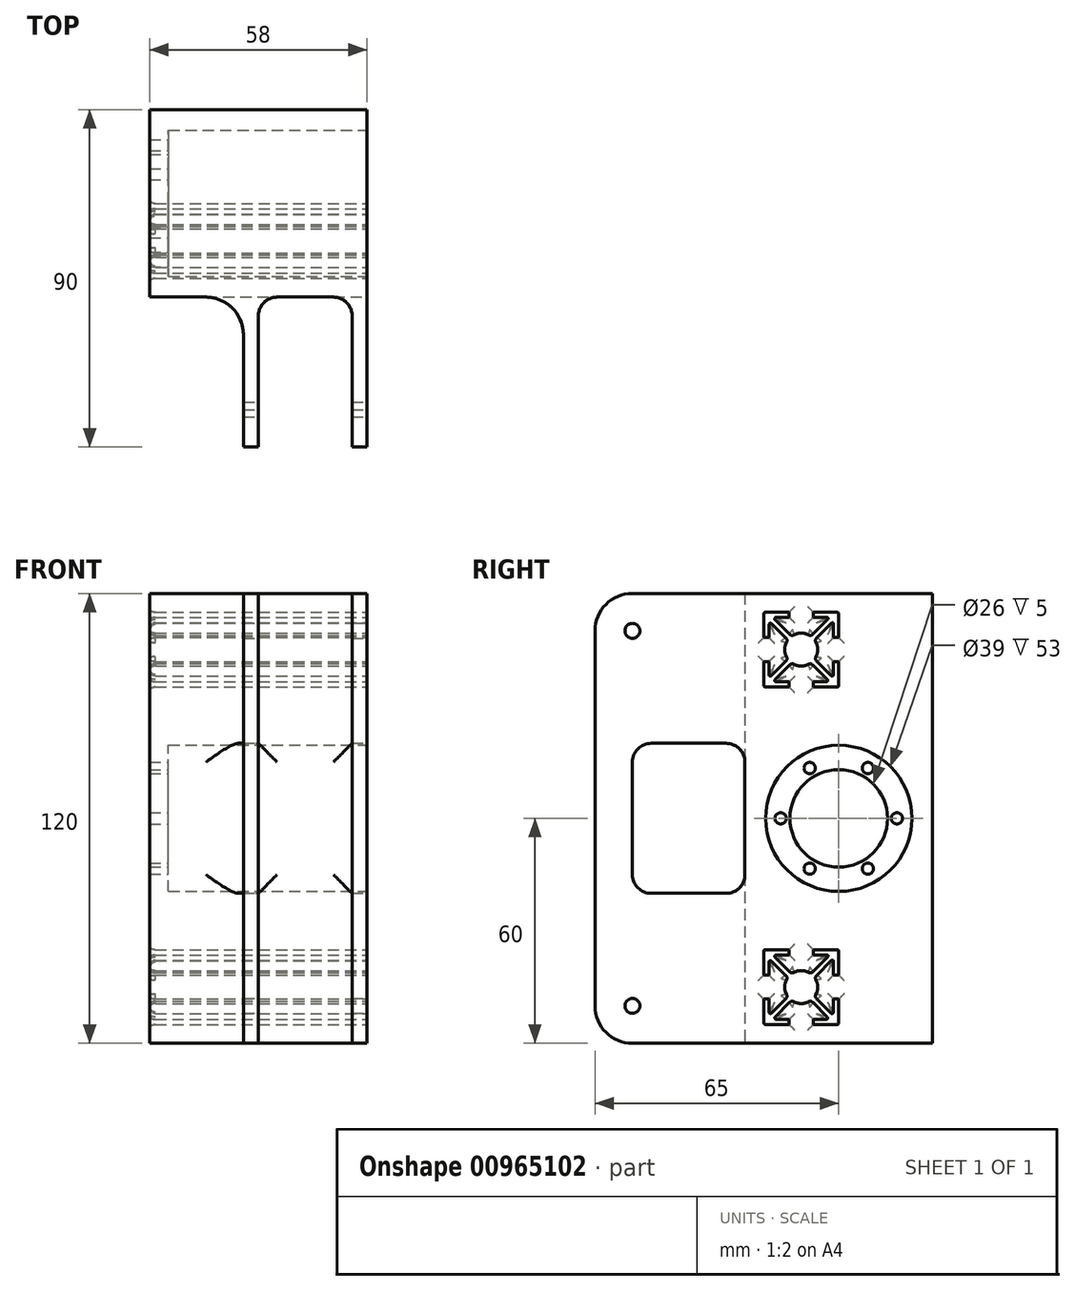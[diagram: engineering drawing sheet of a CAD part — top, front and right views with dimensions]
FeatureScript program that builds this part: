
annotation { "Feature Type Name" : "Feature", "Feature Type Description" : "" }
export const myFeature = defineFeature(function(context is Context, id is Id, definition is map)
    precondition{}
    {
        {
            var Q0;
            Q0=qCreatedBy(makeId("Top.planeOp"),FACE);
            var sketch = newSketch(context, id + "F0", { "sketchPlane" : qUnion([Q0])});
            skLineSegment(sketch, "E0", {"start": v(-25, 90) * mm, "end": v(33, 90) * mm});
            skLineSegment(sketch, "E1", {"start": v(33, 90) * mm, "end": v(33, 0) * mm});
            skLineSegment(sketch, "E2", {"start": v(33, 0) * mm, "end": v(29, 0) * mm});
            skLineSegment(sketch, "E3", {"start": v(29, 0) * mm, "end": v(29, 40) * mm});
            skLineSegment(sketch, "E4", {"start": v(29, 40) * mm, "end": v(4, 40) * mm});
            skLineSegment(sketch, "E5", {"start": v(4, 40) * mm, "end": v(4, 0) * mm});
            skLineSegment(sketch, "E6", {"start": v(4, 0) * mm, "end": v(0, 0) * mm});
            skLineSegment(sketch, "E7", {"start": v(0, 0) * mm, "end": v(0, 40) * mm});
            skLineSegment(sketch, "E8", {"start": v(0, 40) * mm, "end": v(-25, 40) * mm});
            skLineSegment(sketch, "E9", {"start": v(-25, 40) * mm, "end": v(-25, 90) * mm});
            skSolve(sketch);
        }
        {
            var Q0;
            Q0=makeQuery(id+"F0.imprint","IMPRINT",FACE,{"disambiguationData":[TD([[makeQuery(id+"F0.imprint","IMPRINT",EDGE,{"derivedFrom":sQuery(id+"F0.wireOp",EDGE,"VUWFp00N-zC5u-VRxy-L6zH-FIhfyABYxTeX")}),-1.0]])]});
            var Q1;
            Q1=makeQuery(id+"F0.imprint","IMPRINT",FACE,{"disambiguationData":[TD([[makeQuery(id+"F0.imprint","IMPRINT",EDGE,{"derivedFrom":sQuery(id+"F0.wireOp",EDGE,"E0")}),-1.0]])]});
            extrude(context, id + "F1", {"entities" : qUnion([Q0, Q1]), "depth" : 120 * mm, "offsetDistance" : 25 * mm});
        }
        {
            var Q0;
            Q0=makeQuery(id+"F1.opExtrude","SWEPT_FACE",FACE,{"disambiguationData":[OSD([sQuery(id+"F0.wireOp",EDGE,"E1")])]});
            var sketch = newSketch(context, id + "F2", { "sketchPlane" : qUnion([Q0])});
            skCircle(sketch, "E10", {"center": v(10, 110) * mm, "radius": 2 * mm});
            skCircle(sketch, "E11", {"center": v(10, 10) * mm, "radius": 2 * mm});
            skLineSegment(sketch, "E12.bottom", {"start": v(15, 40) * mm, "end": v(35, 40) * mm});
            skLineSegment(sketch, "E12.top", {"start": v(15, 80) * mm, "end": v(35, 80) * mm});
            skLineSegment(sketch, "E12.left", {"start": v(10, 45) * mm, "end": v(10, 75) * mm});
            skLineSegment(sketch, "E12.right", {"start": v(40, 45) * mm, "end": v(40, 75) * mm});
            skPoint(sketch, "E13.visualSharp", {"position": v(10, 40) * mm});
            skArc(sketch, "E13.filletArc", {"start": v(10, 45) * mm, "mid": v(11.46, 41.46) * mm, "end": v(15, 40) * mm});
            skPoint(sketch, "E14.visualSharp", {"position": v(10, 80) * mm});
            skArc(sketch, "E14.filletArc", {"start": v(15, 80) * mm, "mid": v(11.46, 78.54) * mm, "end": v(10, 75) * mm});
            skPoint(sketch, "E15.visualSharp", {"position": v(40, 80) * mm});
            skArc(sketch, "E15.filletArc", {"start": v(40, 75) * mm, "mid": v(38.54, 78.54) * mm, "end": v(35, 80) * mm});
            skPoint(sketch, "E16.visualSharp", {"position": v(40, 40) * mm});
            skArc(sketch, "E16.filletArc", {"start": v(35, 40) * mm, "mid": v(38.54, 41.46) * mm, "end": v(40, 45) * mm});
            skLineSegment(sketch, "E17.bottom", {"start": v(45, 5) * mm, "end": v(65, 5) * mm, "construction": true});
            skLineSegment(sketch, "E17.top", {"start": v(45, 25) * mm, "end": v(65, 25) * mm, "construction": true});
            skLineSegment(sketch, "E17.left", {"start": v(45, 5) * mm, "end": v(45, 25) * mm, "construction": true});
            skLineSegment(sketch, "E17.right", {"start": v(65, 5) * mm, "end": v(65, 25) * mm, "construction": true});
            skLineSegment(sketch, "E18", {"start": v(55, 25) * mm, "end": v(55, 5) * mm, "construction": true});
            skLineSegment(sketch, "E19", {"start": v(65, 15) * mm, "end": v(45, 15) * mm, "construction": true});
            skLineSegment(sketch, "E20", {"start": v(64.5, 25) * mm, "end": v(58.2, 25) * mm});
            skLineSegment(sketch, "E21", {"start": v(58.2, 25) * mm, "end": v(58.2, 23.6) * mm});
            skLineSegment(sketch, "E22", {"start": v(58.2, 23.6) * mm, "end": v(61.89, 23.6) * mm});
            skLineSegment(sketch, "E23", {"start": v(45, 5) * mm, "end": v(65, 25) * mm, "construction": true});
            skLineSegment(sketch, "E24", {"start": v(65, 5) * mm, "end": v(45, 25) * mm, "construction": true});
            skLineSegment(sketch, "E25", {"start": v(62.1, 23.09) * mm, "end": v(58.1, 19.08) * mm});
            skLineSegment(sketch, "E26", {"start": v(65, 18.2) * mm, "end": v(63.6, 18.2) * mm});
            skLineSegment(sketch, "E27", {"start": v(63.6, 18.2) * mm, "end": v(63.6, 21.89) * mm});
            skLineSegment(sketch, "E28", {"start": v(63.09, 22.1) * mm, "end": v(59.08, 18.1) * mm});
            skLineSegment(sketch, "E29", {"start": v(65, 5.5) * mm, "end": v(65, 11.8) * mm});
            skLineSegment(sketch, "E30", {"start": v(65, 11.8) * mm, "end": v(63.6, 11.8) * mm});
            skLineSegment(sketch, "E31", {"start": v(63.6, 11.8) * mm, "end": v(63.6, 8.36) * mm});
            skLineSegment(sketch, "E32", {"start": v(62.92, 8.07) * mm, "end": v(59.08, 11.9) * mm});
            skLineSegment(sketch, "E33", {"start": v(58.2, 5) * mm, "end": v(58.2, 6.4) * mm});
            skLineSegment(sketch, "E34", {"start": v(58.2, 6.4) * mm, "end": v(61.64, 6.4) * mm});
            skLineSegment(sketch, "E35", {"start": v(61.93, 7.08) * mm, "end": v(58.1, 10.92) * mm});
            skLineSegment(sketch, "E36", {"start": v(51.8, 5) * mm, "end": v(51.8, 6.4) * mm});
            skLineSegment(sketch, "E37", {"start": v(51.8, 6.4) * mm, "end": v(48.36, 6.4) * mm});
            skLineSegment(sketch, "E38", {"start": v(48.07, 7.08) * mm, "end": v(51.9, 10.92) * mm});
            skLineSegment(sketch, "E39", {"start": v(51.8, 5) * mm, "end": v(45.5, 5) * mm});
            skLineSegment(sketch, "E40", {"start": v(45, 11.8) * mm, "end": v(46.4, 11.8) * mm});
            skLineSegment(sketch, "E41", {"start": v(46.4, 11.8) * mm, "end": v(46.4, 8.36) * mm});
            skLineSegment(sketch, "E42", {"start": v(47.08, 8.07) * mm, "end": v(50.92, 11.9) * mm});
            skLineSegment(sketch, "E43", {"start": v(45, 24.5) * mm, "end": v(45, 18.2) * mm});
            skLineSegment(sketch, "E44", {"start": v(45, 18.2) * mm, "end": v(46.4, 18.2) * mm});
            skLineSegment(sketch, "E45", {"start": v(46.4, 18.2) * mm, "end": v(46.4, 21.64) * mm});
            skLineSegment(sketch, "E46", {"start": v(47.08, 21.93) * mm, "end": v(50.92, 18.1) * mm});
            skLineSegment(sketch, "E47", {"start": v(51.8, 25) * mm, "end": v(51.8, 23.6) * mm});
            skLineSegment(sketch, "E48", {"start": v(51.8, 23.6) * mm, "end": v(48.36, 23.6) * mm});
            skLineSegment(sketch, "E49", {"start": v(48.07, 22.92) * mm, "end": v(51.9, 19.08) * mm});
            skLineSegment(sketch, "E50", {"start": v(65, 18.2) * mm, "end": v(65, 24.5) * mm});
            skLineSegment(sketch, "E51", {"start": v(51.8, 25) * mm, "end": v(45.5, 25) * mm});
            skLineSegment(sketch, "E52", {"start": v(45, 11.8) * mm, "end": v(45, 5.5) * mm});
            skLineSegment(sketch, "E53", {"start": v(58.2, 5) * mm, "end": v(64.5, 5) * mm});
            skArc(sketch, "E54", {"start": v(56.9, 18.92) * mm, "mid": v(55, 19.41) * mm, "end": v(53.1, 18.92) * mm});
            skArc(sketch, "E55", {"start": v(58.92, 13.1) * mm, "mid": v(59.41, 15) * mm, "end": v(58.92, 16.9) * mm});
            skArc(sketch, "E56", {"start": v(53.1, 11.08) * mm, "mid": v(55, 10.59) * mm, "end": v(56.9, 11.08) * mm});
            skArc(sketch, "E57", {"start": v(51.08, 16.9) * mm, "mid": v(50.59, 15) * mm, "end": v(51.08, 13.1) * mm});
            skPoint(sketch, "E58", {"position": v(55, 15) * mm});
            skPoint(sketch, "E59.visualSharp", {"position": v(47.39, 23.6) * mm});
            skArc(sketch, "E59.filletArc", {"start": v(48.36, 23.6) * mm, "mid": v(47.99, 23.35) * mm, "end": v(48.07, 22.92) * mm});
            skPoint(sketch, "E60.visualSharp", {"position": v(62.61, 23.6) * mm});
            skArc(sketch, "E60.filletArc", {"start": v(62.1, 23.09) * mm, "mid": v(62.16, 23.41) * mm, "end": v(61.89, 23.6) * mm});
            skPoint(sketch, "E61.visualSharp", {"position": v(63.6, 22.61) * mm});
            skArc(sketch, "E61.filletArc", {"start": v(63.6, 21.89) * mm, "mid": v(63.41, 22.16) * mm, "end": v(63.09, 22.1) * mm});
            skPoint(sketch, "E62.visualSharp", {"position": v(63.6, 7.39) * mm});
            skArc(sketch, "E62.filletArc", {"start": v(62.92, 8.07) * mm, "mid": v(63.35, 7.99) * mm, "end": v(63.6, 8.36) * mm});
            skPoint(sketch, "E63.visualSharp", {"position": v(62.61, 6.4) * mm});
            skArc(sketch, "E63.filletArc", {"start": v(61.64, 6.4) * mm, "mid": v(62.01, 6.65) * mm, "end": v(61.93, 7.08) * mm});
            skPoint(sketch, "E64.visualSharp", {"position": v(47.39, 6.4) * mm});
            skArc(sketch, "E64.filletArc", {"start": v(48.07, 7.08) * mm, "mid": v(47.99, 6.65) * mm, "end": v(48.36, 6.4) * mm});
            skPoint(sketch, "E65.visualSharp", {"position": v(46.4, 7.39) * mm});
            skArc(sketch, "E65.filletArc", {"start": v(46.4, 8.36) * mm, "mid": v(46.65, 7.99) * mm, "end": v(47.08, 8.07) * mm});
            skPoint(sketch, "E66.visualSharp", {"position": v(46.4, 22.61) * mm});
            skArc(sketch, "E66.filletArc", {"start": v(47.08, 21.93) * mm, "mid": v(46.65, 22.01) * mm, "end": v(46.4, 21.64) * mm});
            skPoint(sketch, "E67.visualSharp", {"position": v(52.49, 18.5) * mm});
            skArc(sketch, "E67.filletArc", {"start": v(51.9, 19.08) * mm, "mid": v(52.47, 18.8) * mm, "end": v(53.1, 18.92) * mm});
            skPoint(sketch, "E68.visualSharp", {"position": v(57.51, 18.5) * mm});
            skArc(sketch, "E68.filletArc", {"start": v(56.9, 18.92) * mm, "mid": v(57.53, 18.8) * mm, "end": v(58.1, 19.08) * mm});
            skPoint(sketch, "E69.visualSharp", {"position": v(58.5, 17.51) * mm});
            skArc(sketch, "E69.filletArc", {"start": v(59.08, 18.1) * mm, "mid": v(58.8, 17.53) * mm, "end": v(58.92, 16.9) * mm});
            skPoint(sketch, "E70.visualSharp", {"position": v(58.5, 12.49) * mm});
            skArc(sketch, "E70.filletArc", {"start": v(58.92, 13.1) * mm, "mid": v(58.8, 12.47) * mm, "end": v(59.08, 11.9) * mm});
            skPoint(sketch, "E71.visualSharp", {"position": v(57.51, 11.5) * mm});
            skArc(sketch, "E71.filletArc", {"start": v(58.1, 10.92) * mm, "mid": v(57.53, 11.2) * mm, "end": v(56.9, 11.08) * mm});
            skPoint(sketch, "E72.visualSharp", {"position": v(52.49, 11.5) * mm});
            skArc(sketch, "E72.filletArc", {"start": v(53.1, 11.08) * mm, "mid": v(52.47, 11.2) * mm, "end": v(51.9, 10.92) * mm});
            skPoint(sketch, "E73.visualSharp", {"position": v(51.5, 12.49) * mm});
            skArc(sketch, "E73.filletArc", {"start": v(50.92, 11.9) * mm, "mid": v(51.2, 12.47) * mm, "end": v(51.08, 13.1) * mm});
            skPoint(sketch, "E74.visualSharp", {"position": v(51.5, 17.51) * mm});
            skArc(sketch, "E74.filletArc", {"start": v(51.08, 16.9) * mm, "mid": v(51.2, 17.53) * mm, "end": v(50.92, 18.1) * mm});
            skPoint(sketch, "E75.visualSharp", {"position": v(45, 25) * mm});
            skArc(sketch, "E75.filletArc", {"start": v(45.5, 25) * mm, "mid": v(45.15, 24.85) * mm, "end": v(45, 24.5) * mm});
            skPoint(sketch, "E76.visualSharp", {"position": v(65, 25) * mm});
            skArc(sketch, "E76.filletArc", {"start": v(65, 24.5) * mm, "mid": v(64.85, 24.85) * mm, "end": v(64.5, 25) * mm});
            skPoint(sketch, "E77.visualSharp", {"position": v(65, 5) * mm});
            skArc(sketch, "E77.filletArc", {"start": v(64.5, 5) * mm, "mid": v(64.85, 5.15) * mm, "end": v(65, 5.5) * mm});
            skPoint(sketch, "E78.visualSharp", {"position": v(45, 5) * mm});
            skArc(sketch, "E78.filletArc", {"start": v(45, 5.5) * mm, "mid": v(45.15, 5.15) * mm, "end": v(45.5, 5) * mm});
            skLineSegment(sketch, "E79.bottom", {"start": v(45, 95) * mm, "end": v(65, 95) * mm, "construction": true});
            skLineSegment(sketch, "E79.top", {"start": v(45, 115) * mm, "end": v(65, 115) * mm, "construction": true});
            skLineSegment(sketch, "E79.left", {"start": v(45, 95) * mm, "end": v(45, 115) * mm, "construction": true});
            skLineSegment(sketch, "E79.right", {"start": v(65, 95) * mm, "end": v(65, 115) * mm, "construction": true});
            skLineSegment(sketch, "E80", {"start": v(55, 115) * mm, "end": v(55, 95) * mm, "construction": true});
            skLineSegment(sketch, "E81", {"start": v(65, 105) * mm, "end": v(45, 105) * mm, "construction": true});
            skLineSegment(sketch, "E82", {"start": v(64.5, 115) * mm, "end": v(58.2, 115) * mm});
            skLineSegment(sketch, "E83", {"start": v(58.2, 115) * mm, "end": v(58.2, 113.6) * mm});
            skLineSegment(sketch, "E84", {"start": v(58.2, 113.6) * mm, "end": v(61.89, 113.6) * mm});
            skLineSegment(sketch, "E85", {"start": v(45, 95) * mm, "end": v(65, 115) * mm, "construction": true});
            skLineSegment(sketch, "E86", {"start": v(65, 95) * mm, "end": v(45, 115) * mm, "construction": true});
            skLineSegment(sketch, "E87", {"start": v(62.1, 113.09) * mm, "end": v(58.1, 109.08) * mm});
            skLineSegment(sketch, "E88", {"start": v(65, 108.2) * mm, "end": v(63.6, 108.2) * mm});
            skLineSegment(sketch, "E89", {"start": v(63.6, 108.2) * mm, "end": v(63.6, 111.89) * mm});
            skLineSegment(sketch, "E90", {"start": v(63.09, 112.1) * mm, "end": v(59.08, 108.1) * mm});
            skLineSegment(sketch, "E91", {"start": v(65, 95.5) * mm, "end": v(65, 101.8) * mm});
            skLineSegment(sketch, "E92", {"start": v(65, 101.8) * mm, "end": v(63.6, 101.8) * mm});
            skLineSegment(sketch, "E93", {"start": v(63.6, 101.8) * mm, "end": v(63.6, 98.36) * mm});
            skLineSegment(sketch, "E94", {"start": v(62.92, 98.07) * mm, "end": v(59.08, 101.9) * mm});
            skLineSegment(sketch, "E95", {"start": v(58.2, 95) * mm, "end": v(58.2, 96.4) * mm});
            skLineSegment(sketch, "E96", {"start": v(58.2, 96.4) * mm, "end": v(61.64, 96.4) * mm});
            skLineSegment(sketch, "E97", {"start": v(61.93, 97.08) * mm, "end": v(58.1, 100.92) * mm});
            skLineSegment(sketch, "E98", {"start": v(51.8, 95) * mm, "end": v(51.8, 96.4) * mm});
            skLineSegment(sketch, "E99", {"start": v(51.8, 96.4) * mm, "end": v(48.36, 96.4) * mm});
            skLineSegment(sketch, "E100", {"start": v(48.07, 97.08) * mm, "end": v(51.9, 100.92) * mm});
            skLineSegment(sketch, "E101", {"start": v(51.8, 95) * mm, "end": v(45.5, 95) * mm});
            skLineSegment(sketch, "E102", {"start": v(45, 101.8) * mm, "end": v(46.4, 101.8) * mm});
            skLineSegment(sketch, "E103", {"start": v(46.4, 101.8) * mm, "end": v(46.4, 98.36) * mm});
            skLineSegment(sketch, "E104", {"start": v(47.08, 98.07) * mm, "end": v(50.92, 101.9) * mm});
            skLineSegment(sketch, "E105", {"start": v(45, 114.5) * mm, "end": v(45, 108.2) * mm});
            skLineSegment(sketch, "E106", {"start": v(45, 108.2) * mm, "end": v(46.4, 108.2) * mm});
            skLineSegment(sketch, "E107", {"start": v(46.4, 108.2) * mm, "end": v(46.4, 111.64) * mm});
            skLineSegment(sketch, "E108", {"start": v(47.08, 111.93) * mm, "end": v(50.92, 108.1) * mm});
            skLineSegment(sketch, "E109", {"start": v(51.8, 115) * mm, "end": v(51.8, 113.6) * mm});
            skLineSegment(sketch, "E110", {"start": v(51.8, 113.6) * mm, "end": v(48.36, 113.6) * mm});
            skLineSegment(sketch, "E111", {"start": v(48.07, 112.92) * mm, "end": v(51.9, 109.08) * mm});
            skLineSegment(sketch, "E112", {"start": v(65, 108.2) * mm, "end": v(65, 114.5) * mm});
            skLineSegment(sketch, "E113", {"start": v(51.8, 115) * mm, "end": v(45.5, 115) * mm});
            skLineSegment(sketch, "E114", {"start": v(45, 101.8) * mm, "end": v(45, 95.5) * mm});
            skLineSegment(sketch, "E115", {"start": v(58.2, 95) * mm, "end": v(64.5, 95) * mm});
            skArc(sketch, "E116", {"start": v(56.9, 108.92) * mm, "mid": v(55, 109.41) * mm, "end": v(53.1, 108.92) * mm});
            skArc(sketch, "E117", {"start": v(58.92, 103.1) * mm, "mid": v(59.41, 105) * mm, "end": v(58.92, 106.9) * mm});
            skArc(sketch, "E118", {"start": v(53.1, 101.08) * mm, "mid": v(55, 100.59) * mm, "end": v(56.9, 101.08) * mm});
            skArc(sketch, "E119", {"start": v(51.08, 106.9) * mm, "mid": v(50.59, 105) * mm, "end": v(51.08, 103.1) * mm});
            skPoint(sketch, "E120", {"position": v(55, 105) * mm});
            skPoint(sketch, "E121.visualSharp", {"position": v(47.39, 113.6) * mm});
            skArc(sketch, "E121.filletArc", {"start": v(48.36, 113.6) * mm, "mid": v(47.99, 113.35) * mm, "end": v(48.07, 112.92) * mm});
            skPoint(sketch, "E122.visualSharp", {"position": v(62.61, 113.6) * mm});
            skArc(sketch, "E122.filletArc", {"start": v(62.1, 113.09) * mm, "mid": v(62.16, 113.41) * mm, "end": v(61.89, 113.6) * mm});
            skPoint(sketch, "E123.visualSharp", {"position": v(63.6, 112.61) * mm});
            skArc(sketch, "E123.filletArc", {"start": v(63.6, 111.89) * mm, "mid": v(63.41, 112.16) * mm, "end": v(63.09, 112.1) * mm});
            skPoint(sketch, "E124.visualSharp", {"position": v(63.6, 97.39) * mm});
            skArc(sketch, "E124.filletArc", {"start": v(62.92, 98.07) * mm, "mid": v(63.35, 97.99) * mm, "end": v(63.6, 98.36) * mm});
            skPoint(sketch, "E125.visualSharp", {"position": v(62.61, 96.4) * mm});
            skArc(sketch, "E125.filletArc", {"start": v(61.64, 96.4) * mm, "mid": v(62.01, 96.65) * mm, "end": v(61.93, 97.08) * mm});
            skPoint(sketch, "E126.visualSharp", {"position": v(47.39, 96.4) * mm});
            skArc(sketch, "E126.filletArc", {"start": v(48.07, 97.08) * mm, "mid": v(47.99, 96.65) * mm, "end": v(48.36, 96.4) * mm});
            skPoint(sketch, "E127.visualSharp", {"position": v(46.4, 97.39) * mm});
            skArc(sketch, "E127.filletArc", {"start": v(46.4, 98.36) * mm, "mid": v(46.65, 97.99) * mm, "end": v(47.08, 98.07) * mm});
            skPoint(sketch, "E128.visualSharp", {"position": v(46.4, 112.61) * mm});
            skArc(sketch, "E128.filletArc", {"start": v(47.08, 111.93) * mm, "mid": v(46.65, 112.01) * mm, "end": v(46.4, 111.64) * mm});
            skPoint(sketch, "E129.visualSharp", {"position": v(52.49, 108.5) * mm});
            skArc(sketch, "E129.filletArc", {"start": v(51.9, 109.08) * mm, "mid": v(52.47, 108.8) * mm, "end": v(53.1, 108.92) * mm});
            skPoint(sketch, "E130.visualSharp", {"position": v(57.51, 108.5) * mm});
            skArc(sketch, "E130.filletArc", {"start": v(56.9, 108.92) * mm, "mid": v(57.53, 108.8) * mm, "end": v(58.1, 109.08) * mm});
            skPoint(sketch, "E131.visualSharp", {"position": v(58.5, 107.51) * mm});
            skArc(sketch, "E131.filletArc", {"start": v(59.08, 108.1) * mm, "mid": v(58.8, 107.53) * mm, "end": v(58.92, 106.9) * mm});
            skPoint(sketch, "E132.visualSharp", {"position": v(58.5, 102.49) * mm});
            skArc(sketch, "E132.filletArc", {"start": v(58.92, 103.1) * mm, "mid": v(58.8, 102.47) * mm, "end": v(59.08, 101.9) * mm});
            skPoint(sketch, "E133.visualSharp", {"position": v(57.51, 101.5) * mm});
            skArc(sketch, "E133.filletArc", {"start": v(58.1, 100.92) * mm, "mid": v(57.53, 101.2) * mm, "end": v(56.9, 101.08) * mm});
            skPoint(sketch, "E134.visualSharp", {"position": v(52.49, 101.5) * mm});
            skArc(sketch, "E134.filletArc", {"start": v(53.1, 101.08) * mm, "mid": v(52.47, 101.2) * mm, "end": v(51.9, 100.92) * mm});
            skPoint(sketch, "E135.visualSharp", {"position": v(51.5, 102.49) * mm});
            skArc(sketch, "E135.filletArc", {"start": v(50.92, 101.9) * mm, "mid": v(51.2, 102.47) * mm, "end": v(51.08, 103.1) * mm});
            skPoint(sketch, "E136.visualSharp", {"position": v(51.5, 107.51) * mm});
            skArc(sketch, "E136.filletArc", {"start": v(51.08, 106.9) * mm, "mid": v(51.2, 107.53) * mm, "end": v(50.92, 108.1) * mm});
            skPoint(sketch, "E137.visualSharp", {"position": v(45, 115) * mm});
            skArc(sketch, "E137.filletArc", {"start": v(45.5, 115) * mm, "mid": v(45.15, 114.85) * mm, "end": v(45, 114.5) * mm});
            skPoint(sketch, "E138.visualSharp", {"position": v(65, 115) * mm});
            skArc(sketch, "E138.filletArc", {"start": v(65, 114.5) * mm, "mid": v(64.85, 114.85) * mm, "end": v(64.5, 115) * mm});
            skPoint(sketch, "E139.visualSharp", {"position": v(65, 95) * mm});
            skArc(sketch, "E139.filletArc", {"start": v(64.5, 95) * mm, "mid": v(64.85, 95.15) * mm, "end": v(65, 95.5) * mm});
            skPoint(sketch, "E140.visualSharp", {"position": v(45, 95) * mm});
            skArc(sketch, "E140.filletArc", {"start": v(45, 95.5) * mm, "mid": v(45.15, 95.15) * mm, "end": v(45.5, 95) * mm});
            skCircle(sketch, "E141", {"center": v(65, 60) * mm, "radius": 19.5 * mm});
            skCircle(sketch, "E142", {"center": v(65, 60) * mm, "radius": 13 * mm});
            skCircle(sketch, "E143", {"center": v(49.5, 60) * mm, "radius": 1.5 * mm});
            skCircle(sketch, "E144.1.0", {"center": v(57.25, 46.58) * mm, "radius": 1.5 * mm});
            skCircle(sketch, "E144.2.0", {"center": v(72.75, 46.58) * mm, "radius": 1.5 * mm});
            skCircle(sketch, "E144.3.0", {"center": v(80.5, 60) * mm, "radius": 1.5 * mm});
            skCircle(sketch, "E144.4.0", {"center": v(72.75, 73.42) * mm, "radius": 1.5 * mm});
            skCircle(sketch, "E144.5.0", {"center": v(57.25, 73.42) * mm, "radius": 1.5 * mm});
            skLineSegment(sketch, "E145", {"start": v(43.82, 60) * mm, "end": v(87.29, 60) * mm, "construction": true});
            skSolve(sketch);
        }
        {
            var Q0;
            Q0=makeQuery(id+"F2.imprint","IMPRINT",FACE,{"disambiguationData":[TD([[makeQuery(id+"F2.imprint","IMPRINT",EDGE,{"derivedFrom":sQuery(id+"F2.wireOp",EDGE,"E10")}),1.0]])]});
            var Q1;
            Q1=makeQuery(id+"F2.imprint","IMPRINT",FACE,{"disambiguationData":[TD([[makeQuery(id+"F2.imprint","IMPRINT",EDGE,{"derivedFrom":sQuery(id+"F2.wireOp",EDGE,"E11")}),1.0]])]});
            var Q2;
            Q2=makeQuery(id+"F2.imprint","IMPRINT",FACE,{"disambiguationData":[TD([[makeQuery(id+"F2.imprint","IMPRINT",EDGE,{"derivedFrom":sQuery(id+"F2.wireOp",EDGE,"3LTuBmyO-ozfh-fqRh-PIQ7-Bl0UIvrHlnbr")}),1.0]])]});
            var Q3;
            Q3=makeQuery(id+"F2.imprint","IMPRINT",FACE,{"disambiguationData":[TD([[makeQuery(id+"F2.imprint","IMPRINT",EDGE,{"derivedFrom":sQuery(id+"F2.wireOp",EDGE,"pFQCxoCr-TVhD-4vzE-fEfu-qZQpqEUeKmVJ")}),1.0]])]});
            var Q4;
            Q4=makeQuery(id+"F2.imprint","IMPRINT",FACE,{"disambiguationData":[TD([[makeQuery(id+"F2.imprint","IMPRINT",EDGE,{"derivedFrom":sQuery(id+"F2.wireOp",EDGE,"E12.bottom")}),1.0]])]});
            var Q5;
            Q5=makeQuery(id+"F2.imprint","IMPRINT",FACE,{"disambiguationData":[TD([[makeQuery(id+"F2.imprint","IMPRINT",EDGE,{"derivedFrom":sQuery(id+"F2.wireOp",EDGE,"E20")}),1.0]])]});
            var Q6;
            Q6=makeQuery(id+"F2.imprint","IMPRINT",FACE,{"disambiguationData":[TD([[makeQuery(id+"F2.imprint","IMPRINT",EDGE,{"derivedFrom":sQuery(id+"F2.wireOp",EDGE,"E82")}),1.0]])]});
            var Q7;
            Q7=makeQuery(id+"F2.imprint","IMPRINT",FACE,{"disambiguationData":[TD([[makeQuery(id+"F2.imprint","IMPRINT",EDGE,{"derivedFrom":sQuery(id+"F2.wireOp",EDGE,"E142")}),1.0]])]});
            var Q8;
            Q8=makeQuery(id+"F2.imprint","IMPRINT",FACE,{"disambiguationData":[TD([[makeQuery(id+"F2.imprint","IMPRINT",EDGE,{"derivedFrom":sQuery(id+"F2.wireOp",EDGE,"E143")}),1.0]])]});
            var Q9;
            Q9=makeQuery(id+"F2.imprint","IMPRINT",FACE,{"disambiguationData":[TD([[makeQuery(id+"F2.imprint","IMPRINT",EDGE,{"derivedFrom":sQuery(id+"F2.wireOp",EDGE,"E144.7.0")}),1.0]])]});
            var Q10;
            Q10=makeQuery(id+"F2.imprint","IMPRINT",FACE,{"disambiguationData":[TD([[makeQuery(id+"F2.imprint","IMPRINT",EDGE,{"derivedFrom":sQuery(id+"F2.wireOp",EDGE,"E144.6.0")}),1.0]])]});
            var Q11;
            Q11=makeQuery(id+"F2.imprint","IMPRINT",FACE,{"disambiguationData":[TD([[makeQuery(id+"F2.imprint","IMPRINT",EDGE,{"derivedFrom":sQuery(id+"F2.wireOp",EDGE,"E144.5.0")}),1.0]])]});
            var Q12;
            Q12=makeQuery(id+"F2.imprint","IMPRINT",FACE,{"disambiguationData":[TD([[makeQuery(id+"F2.imprint","IMPRINT",EDGE,{"derivedFrom":sQuery(id+"F2.wireOp",EDGE,"E144.4.0")}),1.0]])]});
            var Q13;
            Q13=makeQuery(id+"F2.imprint","IMPRINT",FACE,{"disambiguationData":[TD([[makeQuery(id+"F2.imprint","IMPRINT",EDGE,{"derivedFrom":sQuery(id+"F2.wireOp",EDGE,"E144.3.0")}),1.0]])]});
            var Q14;
            Q14=makeQuery(id+"F2.imprint","IMPRINT",FACE,{"disambiguationData":[TD([[makeQuery(id+"F2.imprint","IMPRINT",EDGE,{"derivedFrom":sQuery(id+"F2.wireOp",EDGE,"E144.2.0")}),1.0]])]});
            var Q15;
            Q15=makeQuery(id+"F2.imprint","IMPRINT",FACE,{"disambiguationData":[TD([[makeQuery(id+"F2.imprint","IMPRINT",EDGE,{"derivedFrom":sQuery(id+"F2.wireOp",EDGE,"E144.1.0")}),1.0]])]});
            extrude(context, id + "F3", {"entities" : qUnion([Q0, Q1, Q2, Q3, Q4, Q5, Q6, Q7, Q8, Q9, Q10, Q11, Q12, Q13, Q14, Q15]), "operationType" : NewBodyOperationType.REMOVE, "oppositeDirection" : true, "depth" : 60 * mm, "offsetDistance" : 25 * mm});
        }
        {
            var Q0;
            Q0=makeQuery(id+"F2.imprint","IMPRINT",FACE,{"disambiguationData":[TD([[makeQuery(id+"F2.imprint","IMPRINT",EDGE,{"derivedFrom":sQuery(id+"F2.wireOp",EDGE,"E141")}),1.0]])]});
            extrude(context, id + "F4", {"entities" : qUnion([Q0]), "operationType" : NewBodyOperationType.REMOVE, "oppositeDirection" : true, "depth" : 53 * mm, "offsetDistance" : 25 * mm});
        }
        {
            var Q0;
            Q0=makeQuery(id+"F1.opExtrude","CAP_EDGE",EDGE,{"disambiguationData":[OSD([sQuery(id+"F0.wireOp",EDGE,"E2")])],"isStart":false});
            var Q1;
            Q1=makeQuery(id+"F1.opExtrude","CAP_EDGE",EDGE,{"disambiguationData":[OSD([sQuery(id+"F0.wireOp",EDGE,"E6")])],"isStart":false});
            var Q2;
            Q2=makeQuery(id+"F1.opExtrude","CAP_EDGE",EDGE,{"disambiguationData":[OSD([sQuery(id+"F0.wireOp",EDGE,"E2")])],"isStart":true});
            var Q3;
            Q3=makeQuery(id+"F1.opExtrude","CAP_EDGE",EDGE,{"disambiguationData":[OSD([sQuery(id+"F0.wireOp",EDGE,"E6")])],"isStart":true});
            var Q4;
            {var subQ0=sQuery(id+"F0.wireOp",EDGE,"E8");var subQ1=sQuery(id+"F0.wireOp",EDGE,"E7");Q4=makeQuery(id+"F3.boolean.opBoolean","SPLIT",EDGE,{"disambiguationData":[TD([makeQuery(id+"F3.opExtrude","SWEPT_FACE",FACE,{"disambiguationData":[OSD([sQuery(id+"F2.wireOp",EDGE,"E15.filletArc")])]})])],"derivedFrom":makeQuery(id+"F1.opExtrude","SWEPT_EDGE",EDGE,{"disambiguationData":[OSD([subQ1,subQ0])]})});}
            var Q5;
            {var subQ0=sQuery(id+"F0.wireOp",EDGE,"E8");var subQ1=sQuery(id+"F0.wireOp",EDGE,"E7");Q5=makeQuery(id+"F3.boolean.opBoolean","SPLIT",EDGE,{"disambiguationData":[TD([makeQuery(id+"F3.opExtrude","SWEPT_FACE",FACE,{"disambiguationData":[OSD([sQuery(id+"F2.wireOp",EDGE,"E16.filletArc")])]})])],"derivedFrom":makeQuery(id+"F1.opExtrude","SWEPT_EDGE",EDGE,{"disambiguationData":[OSD([subQ1,subQ0])]})});}
            fillet(context, id + "F5", {"entities" : qUnion([Q0, Q1, Q2, Q3, Q4, Q5]), "tangentPropagation" : true, "radius" : 10 * mm, "defaultsChanged" : false, "vertexSettings" : [], "allowEdgeOverflow" : false});
        }
        {
            var Q0;
            {var subQ1=sQuery(id+"F0.wireOp",EDGE,"E4");var subQ2=sQuery(id+"F0.wireOp",EDGE,"E5");Q0=makeQuery(id+"F3.boolean.opBoolean","SPLIT",EDGE,{"disambiguationData":[TD([makeQuery(id+"F3.opExtrude","SWEPT_FACE",FACE,{"disambiguationData":[OSD([sQuery(id+"F2.wireOp",EDGE,"E15.filletArc")])]})])],"derivedFrom":makeQuery(id+"F1.opExtrude","SWEPT_EDGE",EDGE,{"disambiguationData":[OSD([subQ1,subQ2])]})});}
            var Q1;
            {var subQ1=sQuery(id+"F0.wireOp",EDGE,"E5");var subQ2=sQuery(id+"F0.wireOp",EDGE,"E4");Q1=makeQuery(id+"F3.boolean.opBoolean","SPLIT",EDGE,{"disambiguationData":[TD([makeQuery(id+"F3.opExtrude","SWEPT_FACE",FACE,{"disambiguationData":[OSD([sQuery(id+"F2.wireOp",EDGE,"E16.filletArc")])]})])],"derivedFrom":makeQuery(id+"F1.opExtrude","SWEPT_EDGE",EDGE,{"disambiguationData":[OSD([subQ2,subQ1])]})});}
            var Q2;
            {var subQ0=sQuery(id+"F0.wireOp",EDGE,"E4");var subQ2=sQuery(id+"F0.wireOp",EDGE,"E3");Q2=makeQuery(id+"F3.boolean.opBoolean","SPLIT",EDGE,{"disambiguationData":[TD([makeQuery(id+"F3.opExtrude","SWEPT_FACE",FACE,{"disambiguationData":[OSD([sQuery(id+"F2.wireOp",EDGE,"E15.filletArc")])]})])],"derivedFrom":makeQuery(id+"F1.opExtrude","SWEPT_EDGE",EDGE,{"disambiguationData":[OSD([subQ2,subQ0])]})});}
            var Q3;
            {var subQ1=sQuery(id+"F0.wireOp",EDGE,"E3");var subQ2=sQuery(id+"F0.wireOp",EDGE,"E4");Q3=makeQuery(id+"F3.boolean.opBoolean","SPLIT",EDGE,{"disambiguationData":[TD([makeQuery(id+"F3.opExtrude","SWEPT_FACE",FACE,{"disambiguationData":[OSD([sQuery(id+"F2.wireOp",EDGE,"E16.filletArc")])]})])],"derivedFrom":makeQuery(id+"F1.opExtrude","SWEPT_EDGE",EDGE,{"disambiguationData":[OSD([subQ1,subQ2])]})});}
            fillet(context, id + "F6", {"entities" : qUnion([Q0, Q1, Q2, Q3]), "tangentPropagation" : true, "radius" : 5 * mm, "defaultsChanged" : false, "vertexSettings" : [], "allowEdgeOverflow" : false});
        }
        {
            var Q0;
            Q0=makeQuery(id+"F3.boolean.opBoolean","INTERSECT",EDGE,{"derivedFrom":[makeQuery(id+"F1.opExtrude","SWEPT_FACE",FACE,{"disambiguationData":[OSD([sQuery(id+"F0.wireOp",EDGE,"E9")])]}),makeQuery(id+"F3.opExtrude","SWEPT_FACE",FACE,{"disambiguationData":[OSD([sQuery(id+"F2.wireOp",EDGE,"E105")])]})]});
            var Q1;
            Q1=makeQuery(id+"F3.boolean.opBoolean","INTERSECT",EDGE,{"derivedFrom":[makeQuery(id+"F1.opExtrude","SWEPT_FACE",FACE,{"disambiguationData":[OSD([sQuery(id+"F0.wireOp",EDGE,"E9")])]}),makeQuery(id+"F3.opExtrude","SWEPT_FACE",FACE,{"disambiguationData":[OSD([sQuery(id+"F2.wireOp",EDGE,"E110")])]})]});
            var Q2;
            Q2=makeQuery(id+"F3.boolean.opBoolean","INTERSECT",EDGE,{"derivedFrom":[makeQuery(id+"F1.opExtrude","SWEPT_FACE",FACE,{"disambiguationData":[OSD([sQuery(id+"F0.wireOp",EDGE,"E9")])]}),makeQuery(id+"F3.opExtrude","SWEPT_FACE",FACE,{"disambiguationData":[OSD([sQuery(id+"F2.wireOp",EDGE,"E108")])]})]});
            var Q3;
            Q3=makeQuery(id+"F3.boolean.opBoolean","INTERSECT",EDGE,{"derivedFrom":[makeQuery(id+"F1.opExtrude","SWEPT_FACE",FACE,{"disambiguationData":[OSD([sQuery(id+"F0.wireOp",EDGE,"E9")])]}),makeQuery(id+"F3.opExtrude","SWEPT_FACE",FACE,{"disambiguationData":[OSD([sQuery(id+"F2.wireOp",EDGE,"E114")])]})]});
            var Q4;
            Q4=makeQuery(id+"F3.boolean.opBoolean","INTERSECT",EDGE,{"derivedFrom":[makeQuery(id+"F1.opExtrude","SWEPT_FACE",FACE,{"disambiguationData":[OSD([sQuery(id+"F0.wireOp",EDGE,"E9")])]}),makeQuery(id+"F3.opExtrude","SWEPT_FACE",FACE,{"disambiguationData":[OSD([sQuery(id+"F2.wireOp",EDGE,"E106")])]})]});
            var Q5;
            Q5=makeQuery(id+"F3.boolean.opBoolean","INTERSECT",EDGE,{"derivedFrom":[makeQuery(id+"F1.opExtrude","SWEPT_FACE",FACE,{"disambiguationData":[OSD([sQuery(id+"F0.wireOp",EDGE,"E9")])]}),makeQuery(id+"F3.opExtrude","SWEPT_FACE",FACE,{"disambiguationData":[OSD([sQuery(id+"F2.wireOp",EDGE,"E109")])]})]});
            var Q6;
            Q6=makeQuery(id+"F3.boolean.opBoolean","INTERSECT",EDGE,{"derivedFrom":[makeQuery(id+"F1.opExtrude","SWEPT_FACE",FACE,{"disambiguationData":[OSD([sQuery(id+"F0.wireOp",EDGE,"E9")])]}),makeQuery(id+"F3.opExtrude","SWEPT_FACE",FACE,{"disambiguationData":[OSD([sQuery(id+"F2.wireOp",EDGE,"E102")])]})]});
            var Q7;
            Q7=makeQuery(id+"F3.boolean.opBoolean","INTERSECT",EDGE,{"derivedFrom":[makeQuery(id+"F1.opExtrude","SWEPT_FACE",FACE,{"disambiguationData":[OSD([sQuery(id+"F0.wireOp",EDGE,"E9")])]}),makeQuery(id+"F3.opExtrude","SWEPT_FACE",FACE,{"disambiguationData":[OSD([sQuery(id+"F2.wireOp",EDGE,"E98")])]})]});
            var Q8;
            Q8=makeQuery(id+"F3.boolean.opBoolean","INTERSECT",EDGE,{"derivedFrom":[makeQuery(id+"F1.opExtrude","SWEPT_FACE",FACE,{"disambiguationData":[OSD([sQuery(id+"F0.wireOp",EDGE,"E9")])]}),makeQuery(id+"F3.opExtrude","SWEPT_FACE",FACE,{"disambiguationData":[OSD([sQuery(id+"F2.wireOp",EDGE,"E99")])]})]});
            var Q9;
            Q9=makeQuery(id+"F3.boolean.opBoolean","INTERSECT",EDGE,{"derivedFrom":[makeQuery(id+"F1.opExtrude","SWEPT_FACE",FACE,{"disambiguationData":[OSD([sQuery(id+"F0.wireOp",EDGE,"E9")])]}),makeQuery(id+"F3.opExtrude","SWEPT_FACE",FACE,{"disambiguationData":[OSD([sQuery(id+"F2.wireOp",EDGE,"E94")])]})]});
            var Q10;
            Q10=makeQuery(id+"F3.boolean.opBoolean","INTERSECT",EDGE,{"derivedFrom":[makeQuery(id+"F1.opExtrude","SWEPT_FACE",FACE,{"disambiguationData":[OSD([sQuery(id+"F0.wireOp",EDGE,"E9")])]}),makeQuery(id+"F3.opExtrude","SWEPT_FACE",FACE,{"disambiguationData":[OSD([sQuery(id+"F2.wireOp",EDGE,"E82")])]})]});
            var Q11;
            Q11=makeQuery(id+"F3.boolean.opBoolean","INTERSECT",EDGE,{"derivedFrom":[makeQuery(id+"F1.opExtrude","SWEPT_FACE",FACE,{"disambiguationData":[OSD([sQuery(id+"F0.wireOp",EDGE,"E9")])]}),makeQuery(id+"F3.opExtrude","SWEPT_FACE",FACE,{"disambiguationData":[OSD([sQuery(id+"F2.wireOp",EDGE,"E83")])]})]});
            var Q12;
            Q12=makeQuery(id+"F3.boolean.opBoolean","INTERSECT",EDGE,{"derivedFrom":[makeQuery(id+"F1.opExtrude","SWEPT_FACE",FACE,{"disambiguationData":[OSD([sQuery(id+"F0.wireOp",EDGE,"E9")])]}),makeQuery(id+"F3.opExtrude","SWEPT_FACE",FACE,{"disambiguationData":[OSD([sQuery(id+"F2.wireOp",EDGE,"E88")])]})]});
            var Q13;
            Q13=makeQuery(id+"F3.boolean.opBoolean","INTERSECT",EDGE,{"derivedFrom":[makeQuery(id+"F1.opExtrude","SWEPT_FACE",FACE,{"disambiguationData":[OSD([sQuery(id+"F0.wireOp",EDGE,"E9")])]}),makeQuery(id+"F3.opExtrude","SWEPT_FACE",FACE,{"disambiguationData":[OSD([sQuery(id+"F2.wireOp",EDGE,"E92")])]})]});
            var Q14;
            Q14=makeQuery(id+"F3.boolean.opBoolean","INTERSECT",EDGE,{"derivedFrom":[makeQuery(id+"F1.opExtrude","SWEPT_FACE",FACE,{"disambiguationData":[OSD([sQuery(id+"F0.wireOp",EDGE,"E9")])]}),makeQuery(id+"F3.opExtrude","SWEPT_FACE",FACE,{"disambiguationData":[OSD([sQuery(id+"F2.wireOp",EDGE,"E91")])]})]});
            var Q15;
            Q15=makeQuery(id+"F3.boolean.opBoolean","INTERSECT",EDGE,{"derivedFrom":[makeQuery(id+"F1.opExtrude","SWEPT_FACE",FACE,{"disambiguationData":[OSD([sQuery(id+"F0.wireOp",EDGE,"E9")])]}),makeQuery(id+"F3.opExtrude","SWEPT_FACE",FACE,{"disambiguationData":[OSD([sQuery(id+"F2.wireOp",EDGE,"E95")])]})]});
            var Q16;
            Q16=makeQuery(id+"F3.boolean.opBoolean","INTERSECT",EDGE,{"derivedFrom":[makeQuery(id+"F1.opExtrude","SWEPT_FACE",FACE,{"disambiguationData":[OSD([sQuery(id+"F0.wireOp",EDGE,"E9")])]}),makeQuery(id+"F3.opExtrude","SWEPT_FACE",FACE,{"disambiguationData":[OSD([sQuery(id+"F2.wireOp",EDGE,"E54")])]})]});
            var Q17;
            Q17=makeQuery(id+"F3.boolean.opBoolean","INTERSECT",EDGE,{"derivedFrom":[makeQuery(id+"F1.opExtrude","SWEPT_FACE",FACE,{"disambiguationData":[OSD([sQuery(id+"F0.wireOp",EDGE,"E9")])]}),makeQuery(id+"F3.opExtrude","SWEPT_FACE",FACE,{"disambiguationData":[OSD([sQuery(id+"F2.wireOp",EDGE,"E57")])]})]});
            var Q18;
            Q18=makeQuery(id+"F3.boolean.opBoolean","INTERSECT",EDGE,{"derivedFrom":[makeQuery(id+"F1.opExtrude","SWEPT_FACE",FACE,{"disambiguationData":[OSD([sQuery(id+"F0.wireOp",EDGE,"E9")])]}),makeQuery(id+"F3.opExtrude","SWEPT_FACE",FACE,{"disambiguationData":[OSD([sQuery(id+"F2.wireOp",EDGE,"E52")])]})]});
            var Q19;
            Q19=makeQuery(id+"F3.boolean.opBoolean","INTERSECT",EDGE,{"derivedFrom":[makeQuery(id+"F1.opExtrude","SWEPT_FACE",FACE,{"disambiguationData":[OSD([sQuery(id+"F0.wireOp",EDGE,"E9")])]}),makeQuery(id+"F3.opExtrude","SWEPT_FACE",FACE,{"disambiguationData":[OSD([sQuery(id+"F2.wireOp",EDGE,"E39")])]})]});
            var Q20;
            Q20=makeQuery(id+"F3.boolean.opBoolean","INTERSECT",EDGE,{"derivedFrom":[makeQuery(id+"F1.opExtrude","SWEPT_FACE",FACE,{"disambiguationData":[OSD([sQuery(id+"F0.wireOp",EDGE,"E9")])]}),makeQuery(id+"F3.opExtrude","SWEPT_FACE",FACE,{"disambiguationData":[OSD([sQuery(id+"F2.wireOp",EDGE,"E36")])]})]});
            var Q21;
            Q21=makeQuery(id+"F3.boolean.opBoolean","INTERSECT",EDGE,{"derivedFrom":[makeQuery(id+"F1.opExtrude","SWEPT_FACE",FACE,{"disambiguationData":[OSD([sQuery(id+"F0.wireOp",EDGE,"E9")])]}),makeQuery(id+"F3.opExtrude","SWEPT_FACE",FACE,{"disambiguationData":[OSD([sQuery(id+"F2.wireOp",EDGE,"E40")])]})]});
            var Q22;
            Q22=makeQuery(id+"F3.boolean.opBoolean","INTERSECT",EDGE,{"derivedFrom":[makeQuery(id+"F1.opExtrude","SWEPT_FACE",FACE,{"disambiguationData":[OSD([sQuery(id+"F0.wireOp",EDGE,"E9")])]}),makeQuery(id+"F3.opExtrude","SWEPT_FACE",FACE,{"disambiguationData":[OSD([sQuery(id+"F2.wireOp",EDGE,"E44")])]})]});
            var Q23;
            Q23=makeQuery(id+"F3.boolean.opBoolean","INTERSECT",EDGE,{"derivedFrom":[makeQuery(id+"F1.opExtrude","SWEPT_FACE",FACE,{"disambiguationData":[OSD([sQuery(id+"F0.wireOp",EDGE,"E9")])]}),makeQuery(id+"F3.opExtrude","SWEPT_FACE",FACE,{"disambiguationData":[OSD([sQuery(id+"F2.wireOp",EDGE,"E43")])]})]});
            var Q24;
            Q24=makeQuery(id+"F3.boolean.opBoolean","INTERSECT",EDGE,{"derivedFrom":[makeQuery(id+"F1.opExtrude","SWEPT_FACE",FACE,{"disambiguationData":[OSD([sQuery(id+"F0.wireOp",EDGE,"E9")])]}),makeQuery(id+"F3.opExtrude","SWEPT_FACE",FACE,{"disambiguationData":[OSD([sQuery(id+"F2.wireOp",EDGE,"E38")])]})]});
            var Q25;
            Q25=makeQuery(id+"F3.boolean.opBoolean","INTERSECT",EDGE,{"derivedFrom":[makeQuery(id+"F1.opExtrude","SWEPT_FACE",FACE,{"disambiguationData":[OSD([sQuery(id+"F0.wireOp",EDGE,"E9")])]}),makeQuery(id+"F3.opExtrude","SWEPT_FACE",FACE,{"disambiguationData":[OSD([sQuery(id+"F2.wireOp",EDGE,"E47")])]})]});
            var Q26;
            Q26=makeQuery(id+"F3.boolean.opBoolean","INTERSECT",EDGE,{"derivedFrom":[makeQuery(id+"F1.opExtrude","SWEPT_FACE",FACE,{"disambiguationData":[OSD([sQuery(id+"F0.wireOp",EDGE,"E9")])]}),makeQuery(id+"F3.opExtrude","SWEPT_FACE",FACE,{"disambiguationData":[OSD([sQuery(id+"F2.wireOp",EDGE,"E55")])]})]});
            var Q27;
            Q27=makeQuery(id+"F3.boolean.opBoolean","INTERSECT",EDGE,{"derivedFrom":[makeQuery(id+"F1.opExtrude","SWEPT_FACE",FACE,{"disambiguationData":[OSD([sQuery(id+"F0.wireOp",EDGE,"E9")])]}),makeQuery(id+"F3.opExtrude","SWEPT_FACE",FACE,{"disambiguationData":[OSD([sQuery(id+"F2.wireOp",EDGE,"E21")])]})]});
            var Q28;
            Q28=makeQuery(id+"F3.boolean.opBoolean","INTERSECT",EDGE,{"derivedFrom":[makeQuery(id+"F1.opExtrude","SWEPT_FACE",FACE,{"disambiguationData":[OSD([sQuery(id+"F0.wireOp",EDGE,"E9")])]}),makeQuery(id+"F3.opExtrude","SWEPT_FACE",FACE,{"disambiguationData":[OSD([sQuery(id+"F2.wireOp",EDGE,"E29")])]})]});
            var Q29;
            Q29=makeQuery(id+"F3.boolean.opBoolean","INTERSECT",EDGE,{"derivedFrom":[makeQuery(id+"F1.opExtrude","SWEPT_FACE",FACE,{"disambiguationData":[OSD([sQuery(id+"F0.wireOp",EDGE,"E9")])]}),makeQuery(id+"F3.opExtrude","SWEPT_FACE",FACE,{"disambiguationData":[OSD([sQuery(id+"F2.wireOp",EDGE,"E33")])]})]});
            var Q30;
            Q30=makeQuery(id+"F3.boolean.opBoolean","INTERSECT",EDGE,{"derivedFrom":[makeQuery(id+"F1.opExtrude","SWEPT_FACE",FACE,{"disambiguationData":[OSD([sQuery(id+"F0.wireOp",EDGE,"E9")])]}),makeQuery(id+"F3.opExtrude","SWEPT_FACE",FACE,{"disambiguationData":[OSD([sQuery(id+"F2.wireOp",EDGE,"E20")])]})]});
            var Q31;
            Q31=makeQuery(id+"F3.boolean.opBoolean","INTERSECT",EDGE,{"derivedFrom":[makeQuery(id+"F1.opExtrude","SWEPT_FACE",FACE,{"disambiguationData":[OSD([sQuery(id+"F0.wireOp",EDGE,"E9")])]}),makeQuery(id+"F3.opExtrude","SWEPT_FACE",FACE,{"disambiguationData":[OSD([sQuery(id+"F2.wireOp",EDGE,"E30")])]})]});
            var Q32;
            Q32=makeQuery(id+"F3.boolean.opBoolean","INTERSECT",EDGE,{"derivedFrom":[makeQuery(id+"F1.opExtrude","SWEPT_FACE",FACE,{"disambiguationData":[OSD([sQuery(id+"F0.wireOp",EDGE,"E9")])]}),makeQuery(id+"F3.opExtrude","SWEPT_FACE",FACE,{"disambiguationData":[OSD([sQuery(id+"F2.wireOp",EDGE,"E26")])]})]});
            var Q33;
            Q33=makeQuery(id+"F3.boolean.opBoolean","INTERSECT",EDGE,{"derivedFrom":[makeQuery(id+"F1.opExtrude","SWEPT_FACE",FACE,{"disambiguationData":[OSD([sQuery(id+"F0.wireOp",EDGE,"E9")])]}),makeQuery(id+"F3.opExtrude","SWEPT_FACE",FACE,{"disambiguationData":[OSD([sQuery(id+"F2.wireOp",EDGE,"E50")])]})]});
            fillet(context, id + "F7", {"entities" : qUnion([Q0, Q1, Q2, Q3, Q4, Q5, Q6, Q7, Q8, Q9, Q10, Q11, Q12, Q13, Q14, Q15, Q16, Q17, Q18, Q19, Q20, Q21, Q22, Q23, Q24, Q25, Q26, Q27, Q28, Q29, Q30, Q31, Q32, Q33]), "tangentPropagation" : true, "crossSection" : FilletCrossSection.CURVATURE, "radius" : 1.5 * mm, "magnitude" : 0.5, "defaultsChanged" : false, "vertexSettings" : []});
        }
    });
